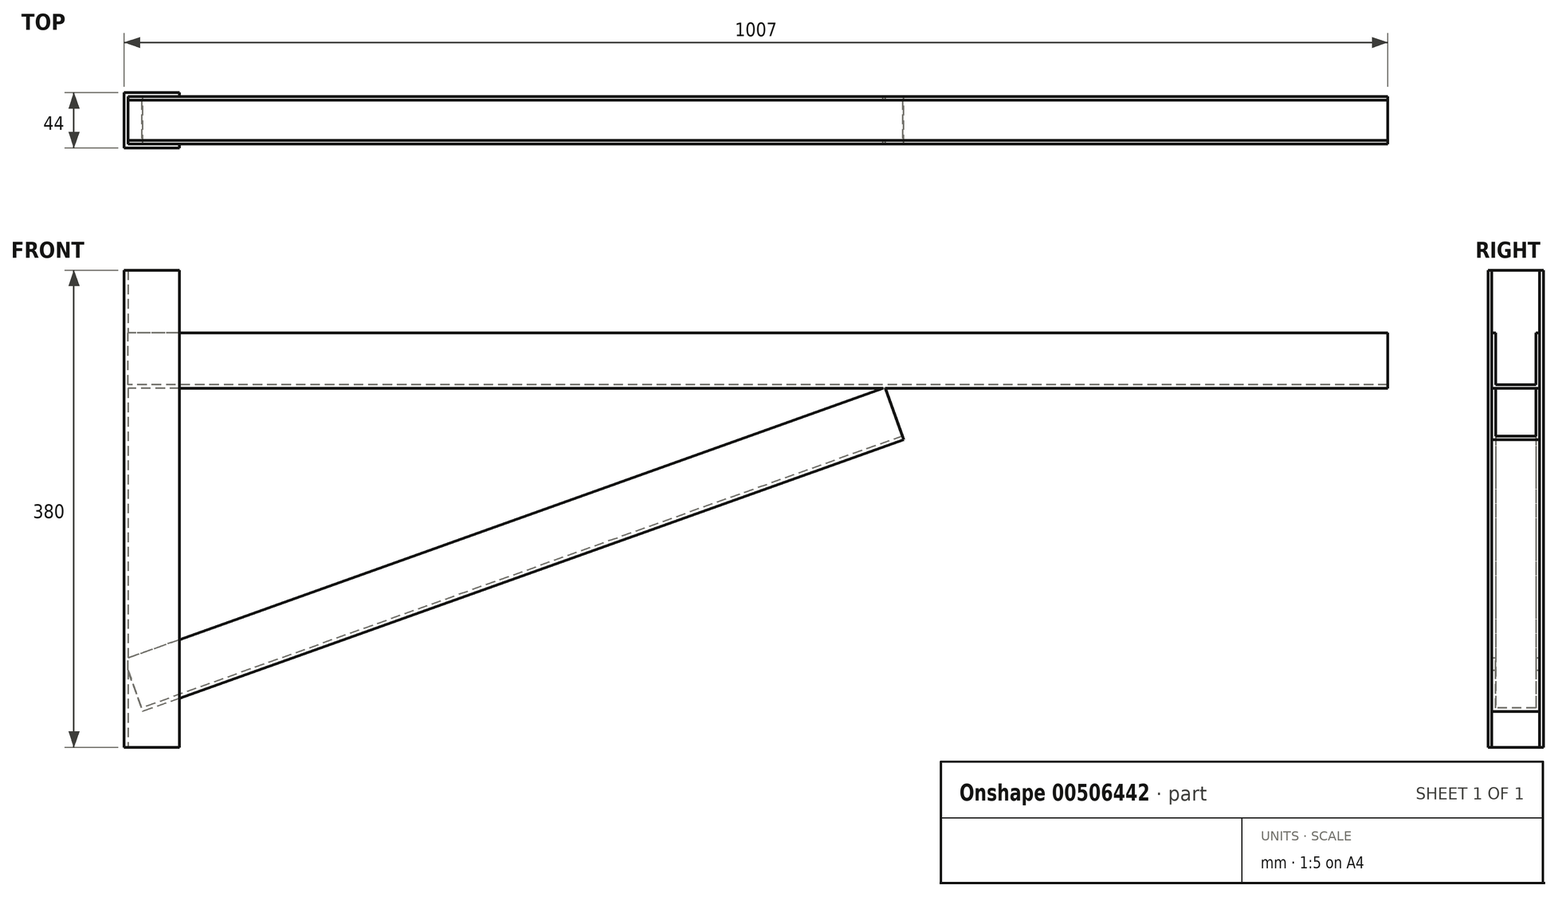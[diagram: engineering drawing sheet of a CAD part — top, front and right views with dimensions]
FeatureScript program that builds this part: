
annotation { "Feature Type Name" : "Feature", "Feature Type Description" : "" }
export const myFeature = defineFeature(function(context is Context, id is Id, definition is map)
    precondition{}
    {
        {
            var Q0;
            Q0=qCreatedBy(makeId("Top.planeOp"),FACE);
            var sketch = newSketch(context, id + "F0", { "sketchPlane" : qUnion([Q0])});
            skLineSegment(sketch, "E0", {"start": v(44, 24.74) * mm, "end": v(0, 24.74) * mm});
            skLineSegment(sketch, "E1", {"start": v(0, 24.74) * mm, "end": v(0, -19.26) * mm});
            skLineSegment(sketch, "E2", {"start": v(0, -19.26) * mm, "end": v(44, -19.26) * mm});
            skLineSegment(sketch, "E3", {"start": v(44, -19.26) * mm, "end": v(44, -16.26) * mm});
            skLineSegment(sketch, "E4", {"start": v(44, -16.26) * mm, "end": v(3, -16.26) * mm});
            skLineSegment(sketch, "E5", {"start": v(3, -16.26) * mm, "end": v(3, 21.74) * mm});
            skLineSegment(sketch, "E6", {"start": v(3, 21.74) * mm, "end": v(44, 21.74) * mm});
            skLineSegment(sketch, "E7", {"start": v(44, 21.74) * mm, "end": v(44, 24.74) * mm});
            skSolve(sketch);
        }
        {
            var Q0;
            Q0 = qSketchRegion(id + "F0", true);
            extrude(context, id + "F1", {"entities" : qUnion([Q0]), "depth" : 380 * mm, "offsetDistance" : 25 * mm});
        }
        {
            var Q0;
            Q0=makeQuery(id+"F1.opExtrude","SWEPT_FACE",FACE,{"disambiguationData":[OSD([sQuery(id+"F0.wireOp",EDGE,"E5")])]});
            var sketch = newSketch(context, id + "F2", { "sketchPlane" : qUnion([Q0])});
            skLineSegment(sketch, "E8", {"start": v(-16.26, 330) * mm, "end": v(-16.26, 286) * mm});
            skLineSegment(sketch, "E9", {"start": v(-16.26, 286) * mm, "end": v(21.74, 286) * mm});
            skLineSegment(sketch, "E10", {"start": v(21.74, 286) * mm, "end": v(21.74, 330) * mm});
            skLineSegment(sketch, "E11", {"start": v(21.74, 330) * mm, "end": v(18.74, 330) * mm});
            skLineSegment(sketch, "E12", {"start": v(18.74, 330) * mm, "end": v(18.74, 289) * mm});
            skLineSegment(sketch, "E13", {"start": v(18.74, 289) * mm, "end": v(-13.26, 289) * mm});
            skLineSegment(sketch, "E14", {"start": v(-13.26, 289) * mm, "end": v(-13.26, 330) * mm});
            skLineSegment(sketch, "E15", {"start": v(-13.26, 330) * mm, "end": v(-16.26, 330) * mm});
            skSolve(sketch);
        }
        {
            var Q0;
            Q0 = qSketchRegion(id + "F2", true);
            extrude(context, id + "F3", {"entities" : qUnion([Q0]), "operationType" : NewBodyOperationType.ADD, "depth" : 1004 * mm, "offsetDistance" : 25 * mm});
        }
        {
            var Q0;
            Q0=makeQuery(id+"F1.opExtrude","SWEPT_FACE",FACE,{"disambiguationData":[OSD([sQuery(id+"F0.wireOp",EDGE,"E1")])]});
            var sketch = newSketch(context, id + "F4", { "sketchPlane" : qUnion([Q0])});
            skLineSegment(sketch, "E16", {"start": v(-24.74, 70) * mm, "end": v(19.26, 70) * mm, "construction": true});
            skSolve(sketch);
        }
        {
            var Q0;
            Q0=qCreatedBy(makeId("Top.planeOp"),FACE);
            var sketch = newSketch(context, id + "F5", { "sketchPlane" : qUnion([Q0])});
            skLineSegment(sketch, "E17", {"start": v(25, 10.43) * mm, "end": v(25, -11.32) * mm, "construction": true});
            skSolve(sketch);
        }
        {
            var Q0;
            Q0 = qBodyType(qCreatedBy(id + "F4" ,EDGE), BodyType.WIRE);
            var Q1;
            Q1 = qBodyType(qCreatedBy(id + "F5" ,EDGE), BodyType.WIRE);
            cPlane(context, id + "F6", {"entities" : qUnion([Q0, Q1]), "cplaneType" : CPlaneType.LINE_ANGLE, "offset" : 25 * mm, "angle" : 0 * degree, "width" : 150 * mm, "height" : 150 * mm});
        }
        {
            var Q0;
            Q0=qCreatedBy(id+"F6.planeOp",FACE);
            var sketch = newSketch(context, id + "F7", { "sketchPlane" : qUnion([Q0])});
            skLineSegment(sketch, "E18", {"start": v(-16.26, 65.92) * mm, "end": v(-16.26, 21.92) * mm});
            skLineSegment(sketch, "E19", {"start": v(-16.26, 21.92) * mm, "end": v(21.74, 21.92) * mm});
            skLineSegment(sketch, "E20", {"start": v(21.74, 21.92) * mm, "end": v(21.74, 65.92) * mm});
            skLineSegment(sketch, "E21", {"start": v(21.74, 65.92) * mm, "end": v(18.74, 65.92) * mm});
            skLineSegment(sketch, "E22", {"start": v(18.74, 65.92) * mm, "end": v(18.74, 24.92) * mm});
            skLineSegment(sketch, "E23", {"start": v(18.74, 24.92) * mm, "end": v(-13.26, 24.92) * mm});
            skLineSegment(sketch, "E24", {"start": v(-13.26, 24.92) * mm, "end": v(-13.26, 65.92) * mm});
            skLineSegment(sketch, "E25", {"start": v(-13.26, 65.92) * mm, "end": v(-16.26, 65.92) * mm});
            skSolve(sketch);
        }
        {
            var Q0;
            Q0 = qSketchRegion(id + "F7", true);
            var Q1;
            Q1=makeQuery(id+"F3.opExtrude","SWEPT_FACE",FACE,{"disambiguationData":[OSD([sQuery(id+"F2.wireOp",EDGE,"E9")])]});
            extrude(context, id + "F8", {"entities" : qUnion([Q0]), "operationType" : NewBodyOperationType.ADD, "depth" : 644 * mm, "endBoundEntityFace" : qUnion([Q1]), "offsetDistance" : 25 * mm});
        }
    });
